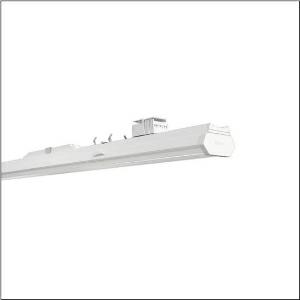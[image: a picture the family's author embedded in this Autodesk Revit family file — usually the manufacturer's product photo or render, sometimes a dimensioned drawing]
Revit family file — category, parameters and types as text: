
# Revit family: licross_r__11_protected_ho_51tp12cn4dxl_0746
name_source: partatom
category: Lighting Fixtures
units: mm (PartAtom-declared; Revit-internal decimal feet)

## family parameters
Cut with Voids When Loaded = No
Host = Face
Light Source = No
Part Type = Normal
Room Calculation Point = No
Round Connector Dimension = Use Diameter
Shared = No

## types (1)
- --- (1 x LED, 13270 lm, 78.7 W, 4000K)
    Apparent Load = 79 VA
    CIE Flux Codes = 70 91 97 98 100
    Color Rendering = 80
    Color Temperature = 4000K
    Default Elevation = 1800 mm
    Description = Licross® 11 Protected HOluminaire insert, length: 1.500mm, width: 90mm, height: 101mm, LED rated luminous flux: 13.270lm, light colour: 840, control gear: ON/OFF Multilumen, CLOi, control gear: ECG Multilumen, with plug, 3-pole, with phase selection, mains connection: 220..240V, AC, 50/60Hz, halogen-free wiring, primary optical cover: cover, of PMMA, light emission: direct with ceiling illumination distribution, protection rating (complete): IP64, insulation class (complete): insulation class I (protective earthing), certification: CE, ENEC, VDE, protection symbol: D if used in an environment with conductive dust loads with corresponding accessories, permissible ambient temperature for indoor applications: -35..+40°C, reducing of maximum allowable ambient temperature of 5°C with ceiling mounting, corresponds to IFS (International Featured Standards) requirements for safety and quality in the food industry, packaging unit: 1 piece
    Height = 92 mm
    Lamp = 1 x LED
    Lamp Light Flux = 13270 lm
    Lamp Power = 78.7 W
    Lamp count = 1
    Length = 1500 mm
    Luminous efficacy = 169 lm/W
    Manufacturer = Siteco
    ModVariant = No
    Model = 51TP12CN4DXL
    Mounting Place = Ceiling
    Mounting Type = Pendant
    Number of Poles = 1
    OnlyDefault = Yes
    Power Factor = 1
    Product Name = Licross® 11 Protected HO
    Product group = luminaire insert
    ProductGroupID = 902
    Protection Class = Protection class I
    Protection Degree = IP 64
    RLX_Detail_Level = 1
    RlxData = <blob elided: 21817 chars, md5=c8c98d03>
    Socket = socket
    Standby Power = 0 W
    System Light Flux = 13270 lm
    System Power = 79 W
    Type Comments = factory setting: luminous flux: 100 % | (A | C | E) | 182 mA
    Type Image = l_1256148.jpg
    URL = http://relux.com
    VarID = @adj_138049
    Voltage = 0 V
    Weight = 0.00 kg
    Width = 88 mm

## geometry (parser evidence)
native form markers: Blend x4, Sweep x9
no freeform markers — native parametric forms only
